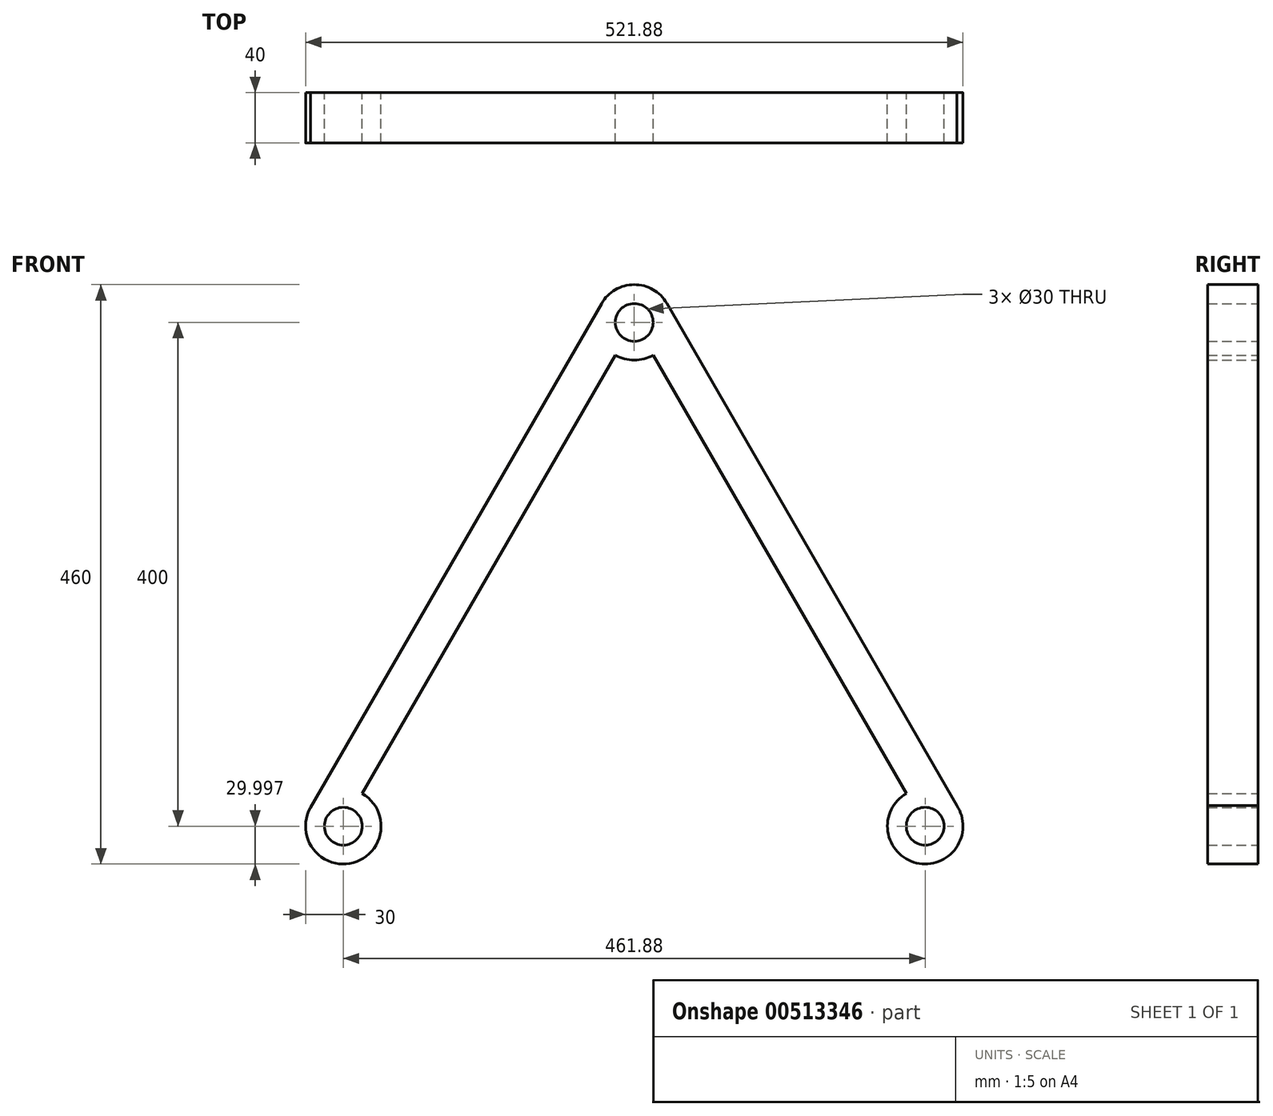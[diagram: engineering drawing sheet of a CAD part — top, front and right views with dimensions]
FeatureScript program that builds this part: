
annotation { "Feature Type Name" : "Feature", "Feature Type Description" : "" }
export const myFeature = defineFeature(function(context is Context, id is Id, definition is map)
    precondition{}
    {
        {
            var Q0;
            Q0=qCreatedBy(makeId("Front.planeOp"),FACE);
            var sketch = newSketch(context, id + "F0", { "sketchPlane" : qUnion([Q0])});
            skLineSegment(sketch, "E0.0", {"start": v(230.94, -133.33) * mm, "end": v(-230.94, -133.33) * mm, "construction": true});
            skLineSegment(sketch, "E0.1", {"start": v(-230.94, -133.33) * mm, "end": v(0, 266.67) * mm, "construction": true});
            skLineSegment(sketch, "E0.2", {"start": v(0, 266.67) * mm, "end": v(230.94, -133.33) * mm, "construction": true});
            skPoint(sketch, "E0.0.midPoint", {"position": v(0, -133.33) * mm});
            skCircle(sketch, "E1", {"center": v(0, 266.67) * mm, "radius": 15 * mm});
            skCircle(sketch, "E2", {"center": v(230.94, -133.33) * mm, "radius": 15 * mm});
            skCircle(sketch, "E3", {"center": v(-230.94, -133.33) * mm, "radius": 15 * mm});
            skCircle(sketch, "E4", {"center": v(-230.94, -133.33) * mm, "radius": 30 * mm});
            skCircle(sketch, "E5", {"center": v(0, 266.67) * mm, "radius": 30 * mm});
            skCircle(sketch, "E6", {"center": v(230.94, -133.33) * mm, "radius": 30 * mm});
            skLineSegment(sketch, "E7", {"start": v(-231.3, -163.92) * mm, "end": v(230.98, -163.33) * mm});
            skLineSegment(sketch, "E8", {"start": v(-257.09, -118.62) * mm, "end": v(-25.98, 281.67) * mm});
            skLineSegment(sketch, "E9", {"start": v(25.86, 281.87) * mm, "end": v(256, -116.83) * mm});
            skLineSegment(sketch, "E10", {"start": v(-200.94, -133.33) * mm, "end": v(200.94, -133.33) * mm});
            skLineSegment(sketch, "E11", {"start": v(215.94, -107.35) * mm, "end": v(15, 240.69) * mm});
            skLineSegment(sketch, "E12", {"start": v(-15, 240.69) * mm, "end": v(-215.94, -107.35) * mm});
            skSolve(sketch);
        }
        {
            var Q0;
            {var subQ0=sQuery(id+"F0.wireOp",EDGE,"E12");Q0=makeQuery(id+"F0.imprint","IMPRINT",FACE,{"disambiguationData":[TD([[makeQuery(id+"F0.imprint","IMPRINT",EDGE,{"derivedFrom":subQ0}),-1.0]])]});}
            var Q1;
            Q1=makeQuery(id+"F0.imprint","IMPRINT",FACE,{"disambiguationData":[TD([[makeQuery(id+"F0.imprint","IMPRINT",EDGE,{"derivedFrom":sQuery(id+"F0.wireOp",EDGE,"E3")}),-1.0]])]});
            var Q2;
            Q2=makeQuery(id+"F0.imprint","IMPRINT",FACE,{"disambiguationData":[TD([[makeQuery(id+"F0.imprint","IMPRINT",EDGE,{"derivedFrom":sQuery(id+"F0.wireOp",EDGE,"E1")}),-1.0]])]});
            var Q3;
            {var subQ0=sQuery(id+"F0.wireOp",EDGE,"E11");Q3=makeQuery(id+"F0.imprint","IMPRINT",FACE,{"disambiguationData":[TD([[makeQuery(id+"F0.imprint","IMPRINT",EDGE,{"derivedFrom":subQ0}),-1.0]])]});}
            var Q4;
            Q4=makeQuery(id+"F0.imprint","IMPRINT",FACE,{"disambiguationData":[TD([[makeQuery(id+"F0.imprint","IMPRINT",EDGE,{"derivedFrom":sQuery(id+"F0.wireOp",EDGE,"E2")}),-1.0]])]});
            extrude(context, id + "F1", {"entities" : qUnion([Q0, Q1, Q2, Q3, Q4]), "depth" : 40 * mm});
        }
    });
